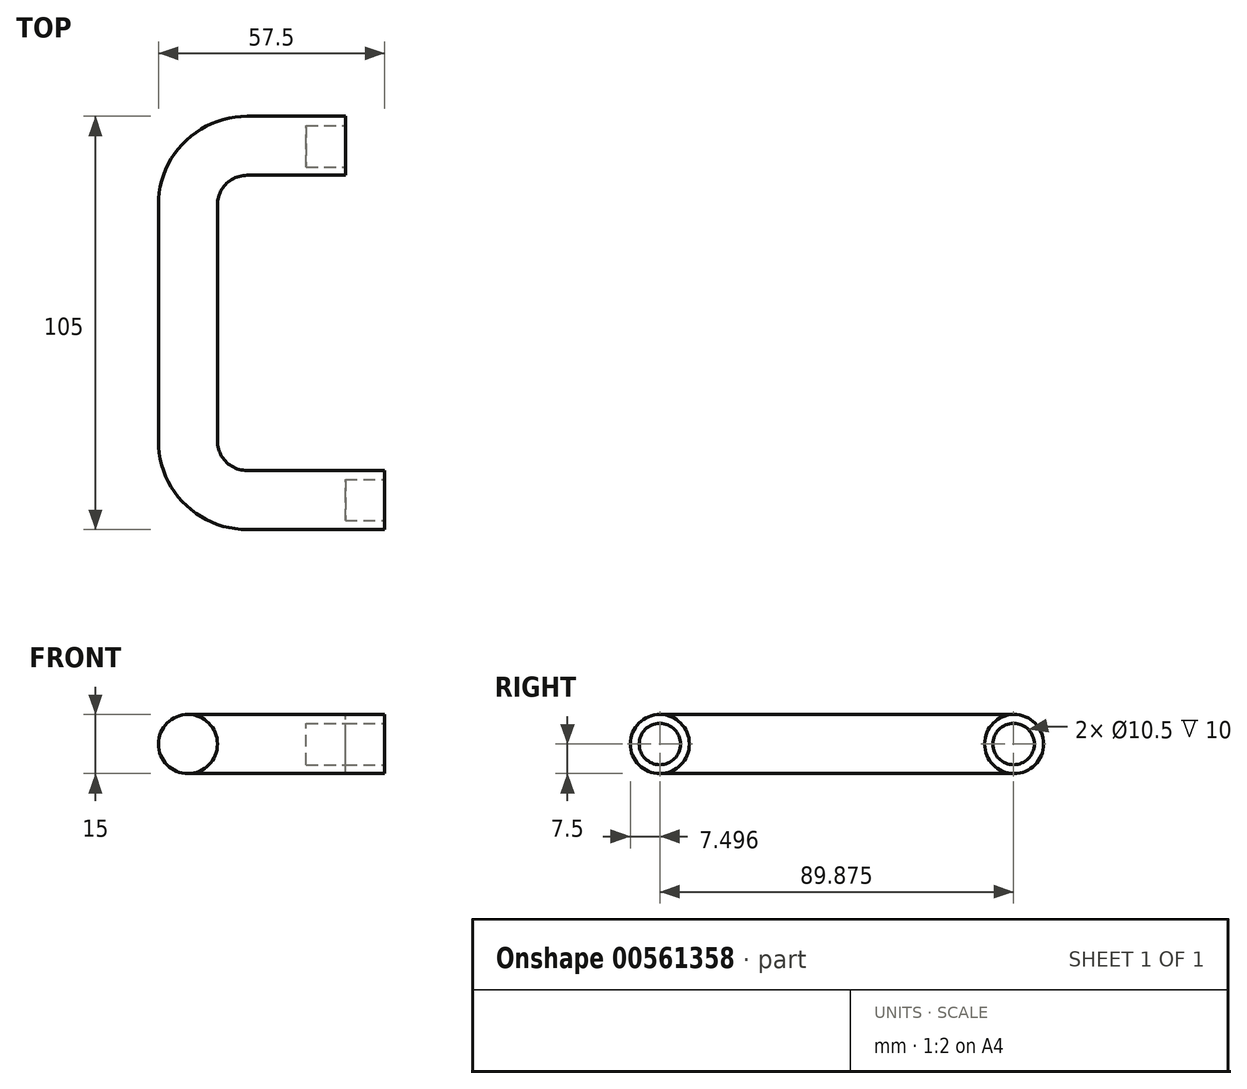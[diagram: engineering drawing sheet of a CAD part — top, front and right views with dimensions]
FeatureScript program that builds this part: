
annotation { "Feature Type Name" : "Feature", "Feature Type Description" : "" }
export const myFeature = defineFeature(function(context is Context, id is Id, definition is map)
    precondition{}
    {
        {
            var Q0;
            Q0=qCreatedBy(makeId("Right.planeOp"),FACE);
            var sketch = newSketch(context, id + "F0", { "sketchPlane" : qUnion([Q0])});
            skCircle(sketch, "E0", {"center": v(-20.43, 0) * mm, "radius": 7.5 * mm});
            skCircle(sketch, "E1", {"center": v(69.57, 0) * mm, "radius": 7.5 * mm});
            skSolve(sketch);
        }
        {
            var Q0;
            Q0=qCreatedBy(makeId("Top.planeOp"),FACE);
            var sketch = newSketch(context, id + "F1", { "sketchPlane" : qUnion([Q0])});
            skLineSegment(sketch, "E2", {"start": v(0, -20.43) * mm, "end": v(-25, -20.43) * mm});
            skLineSegment(sketch, "E3", {"start": v(-40, -5.43) * mm, "end": v(-40, 54.57) * mm});
            skLineSegment(sketch, "E4", {"start": v(-25, 69.57) * mm, "end": v(0, 69.57) * mm});
            skPoint(sketch, "E5.visualSharp", {"position": v(-40, 69.57) * mm});
            skArc(sketch, "E5.filletArc", {"start": v(-25, 69.57) * mm, "mid": v(-35.6, 65.17) * mm, "end": v(-40, 54.57) * mm});
            skPoint(sketch, "E6.visualSharp", {"position": v(-40, -20.43) * mm});
            skArc(sketch, "E6.filletArc", {"start": v(-40, -5.43) * mm, "mid": v(-35.6, -16.04) * mm, "end": v(-25, -20.43) * mm});
            skSolve(sketch);
        }
        {
            var Q0;
            Q0=makeQuery(id+"F0.imprint","IMPRINT",FACE,{"disambiguationData":[TD([[makeQuery(id+"F0.imprint","IMPRINT",EDGE,{"derivedFrom":sQuery(id+"F0.wireOp",EDGE,"E1")}),1.0]])]});
            var Q1;
            Q1=sQuery(id+"F1.wireOp",EDGE,"E2");
            var Q2;
            Q2=sQuery(id+"F1.wireOp",EDGE,"E6.filletArc");
            var Q3;
            Q3=sQuery(id+"F1.wireOp",EDGE,"E3");
            var Q4;
            Q4=sQuery(id+"F1.wireOp",EDGE,"E5.filletArc");
            var Q5;
            Q5=sQuery(id+"F1.wireOp",EDGE,"E4");
            sweep(context, id + "F2", {"profiles" : qUnion([Q0]), "path" : qUnion([Q1, Q2, Q3, Q4, Q5])});
        }
        {
            var Q0;
            Q0=makeQuery(id+"F0.imprint","IMPRINT",FACE,{"disambiguationData":[TD([[makeQuery(id+"F0.imprint","IMPRINT",EDGE,{"derivedFrom":sQuery(id+"F0.wireOp",EDGE,"E0")}),1.0]])]});
            var sketch = newSketch(context, id + "F3", { "sketchPlane" : qUnion([Q0])});
            skCircle(sketch, "E7.0", {"center": v(-20.43, 0) * mm, "radius": 7.5 * mm});
            skSolve(sketch);
        }
        {
            var Q0;
            Q0 = qSketchRegion(id + "F3", true);
            extrude(context, id + "F4", {"entities" : qUnion([Q0]), "operationType" : NewBodyOperationType.ADD, "depth" : 10 * mm, "offsetDistance" : 25 * mm});
        }
        {
            var Q0;
            Q0=makeQuery(id+"F4.opExtrude","CAP_FACE",FACE,{"disambiguationData":[OSD([sQuery(id+"F3.wireOp",EDGE,"E7.0")])],"isStart":false});
            var sketch = newSketch(context, id + "F5", { "sketchPlane" : qUnion([Q0])});
            skCircle(sketch, "E8", {"center": v(-20.43, 0) * mm, "radius": 5.25 * mm});
            skSolve(sketch);
        }
        {
            var Q0;
            Q0 = qSketchRegion(id + "F5", true);
            extrude(context, id + "F6", {"entities" : qUnion([Q0]), "operationType" : NewBodyOperationType.REMOVE, "oppositeDirection" : true, "depth" : 10 * mm, "offsetDistance" : 25 * mm});
        }
        {
            var Q0;
            Q0=makeQuery(id+"F0.imprint","IMPRINT",FACE,{"disambiguationData":[TD([[makeQuery(id+"F0.imprint","IMPRINT",EDGE,{"derivedFrom":sQuery(id+"F0.wireOp",EDGE,"E1")}),1.0]])]});
            var sketch = newSketch(context, id + "F7", { "sketchPlane" : qUnion([Q0])});
            skCircle(sketch, "E9", {"center": v(69.44, 0) * mm, "radius": 5.25 * mm});
            skSolve(sketch);
        }
        {
            var Q0;
            Q0 = qSketchRegion(id + "F7", true);
            extrude(context, id + "F8", {"entities" : qUnion([Q0]), "operationType" : NewBodyOperationType.REMOVE, "oppositeDirection" : true, "depth" : 10 * mm, "offsetDistance" : 25 * mm});
        }
    });
